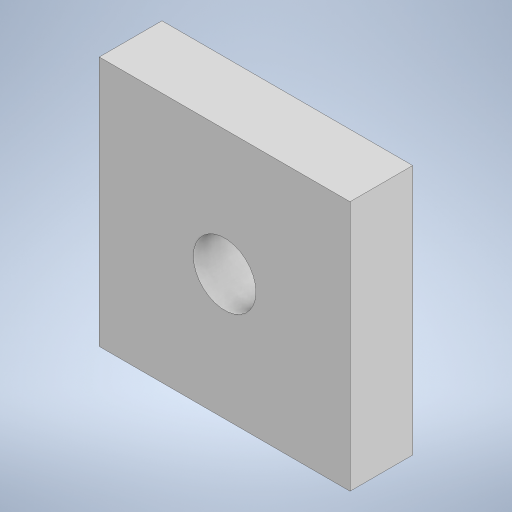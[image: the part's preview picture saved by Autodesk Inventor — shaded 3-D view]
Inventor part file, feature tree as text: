
AUTODESK INVENTOR PART (.ipt)
format: ipt  version: 2023 (Build 270158000, 158)  size: 249,344 bytes
history: native  units: in
note: dims shown in document units (in); Inventor stores cm internally (conversion verified against a paired STEP export)
features: extrude x1, sketch x1
ambient origin geometry x8: Origin, YZ Plane, XZ Plane, XY Plane, X Axis, Y Axis, Z Axis, Center Point
bodies: Body1 (feature_tree)
feature tree (2):
  extrude  "Extrusion2"  Depth=0.7874in
  sketch  "Sketch1"  dims[d0=0.7874in d1=0.7874in d5=0.3937in d6=0.3937in d7=0.1969in d8=0.1969in d9=0.0in]
